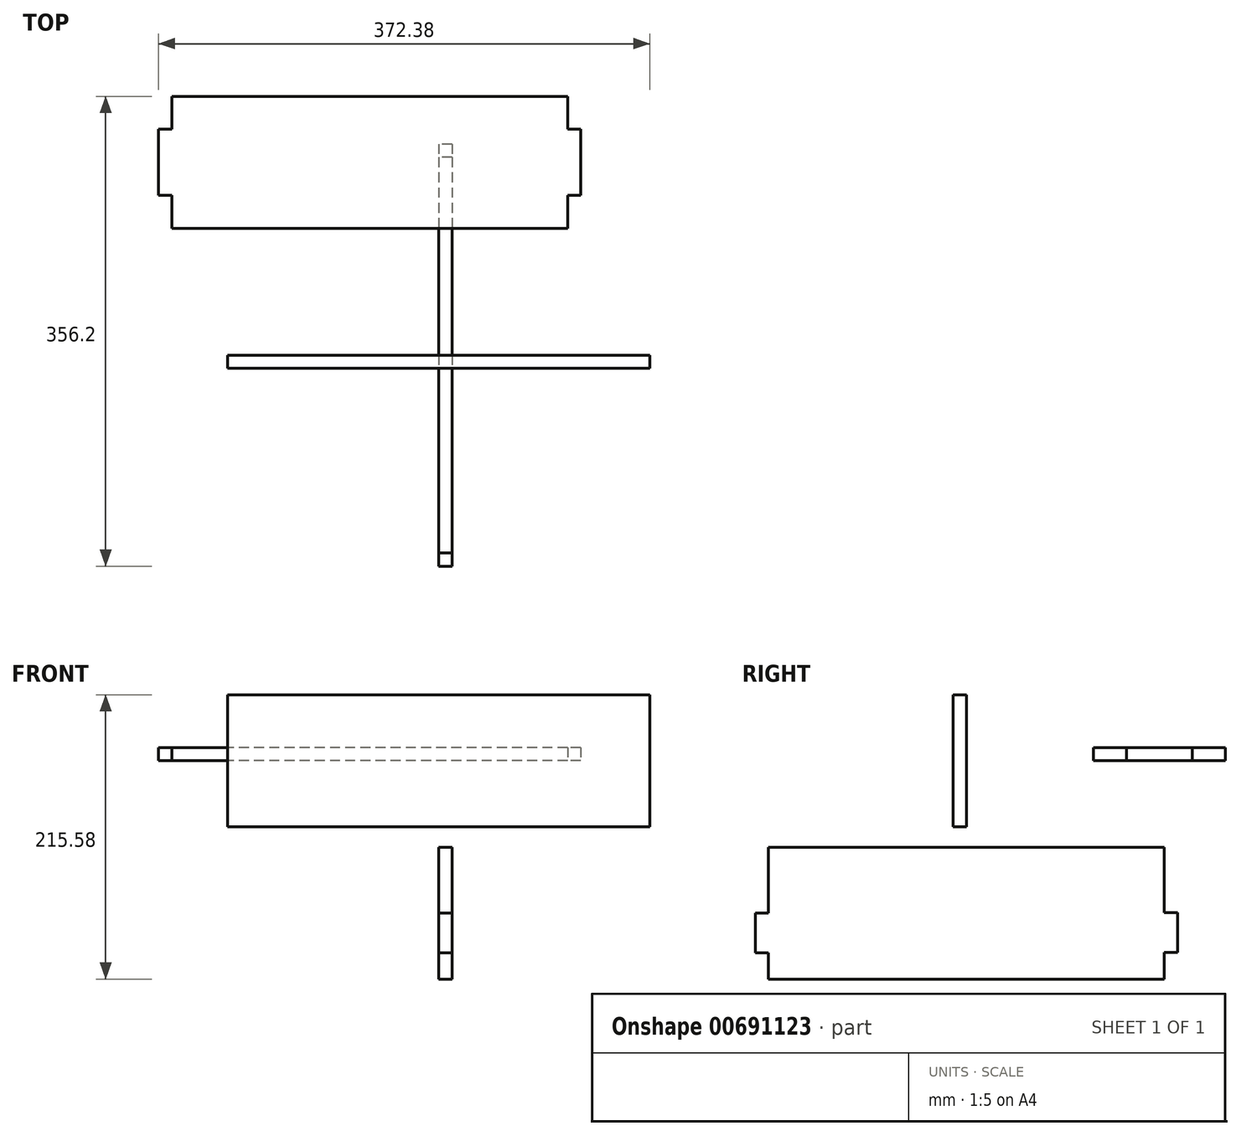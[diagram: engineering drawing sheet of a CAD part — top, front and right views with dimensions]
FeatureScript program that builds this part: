
annotation { "Feature Type Name" : "Feature", "Feature Type Description" : "" }
export const myFeature = defineFeature(function(context is Context, id is Id, definition is map)
    precondition{}
    {
        {
            var Q0;
            Q0=qCreatedBy(makeId("Front.planeOp"),FACE);
            var sketch = newSketch(context, id + "F0", { "sketchPlane" : qUnion([Q0])});
            skLineSegment(sketch, "E0.bottom", {"start": v(160, -50) * mm, "end": v(-160, -50) * mm});
            skLineSegment(sketch, "E0.top", {"start": v(160, 50) * mm, "end": v(-160, 50) * mm});
            skLineSegment(sketch, "E0.left", {"start": v(160, -50) * mm, "end": v(160, 50) * mm});
            skLineSegment(sketch, "E0.right", {"start": v(-160, -50) * mm, "end": v(-160, 50) * mm});
            skPoint(sketch, "E0.middle", {"position": v(0, 0) * mm});
            skSolve(sketch);
        }
        {
            var Q0;
            Q0=makeQuery(id+"F0.imprint","IMPRINT",FACE,{"disambiguationData":[TD([[makeQuery(id+"F0.imprint","IMPRINT",EDGE,{"derivedFrom":sQuery(id+"F0.wireOp",EDGE,"E0.bottom")}),-1.0]])]});
            extrude(context, id + "F1", {"entities" : qUnion([Q0]), "depth" : 10 * mm, "offsetDistance" : 25 * mm});
        }
        {
            var Q0;
            Q0=qCreatedBy(makeId("Top.planeOp"),FACE);
            var sketch = newSketch(context, id + "F2", { "sketchPlane" : qUnion([Q0])});
            skLineSegment(sketch, "E1.bottom", {"start": v(107.62, 96.25) * mm, "end": v(-212.38, 96.25) * mm});
            skLineSegment(sketch, "E1.top", {"start": v(107.62, 196.25) * mm, "end": v(-212.38, 196.25) * mm});
            skLineSegment(sketch, "E1.left", {"start": v(107.62, 96.25) * mm, "end": v(107.62, 196.25) * mm});
            skLineSegment(sketch, "E1.right", {"start": v(-212.38, 96.25) * mm, "end": v(-212.38, 196.25) * mm});
            skPoint(sketch, "E1.middle", {"position": v(-52.38, 146.25) * mm});
            skLineSegment(sketch, "E2", {"start": v(-202.38, 196.25) * mm, "end": v(-202.38, 96.25) * mm});
            skLineSegment(sketch, "E3", {"start": v(97.62, 196.25) * mm, "end": v(97.62, 96.25) * mm});
            skLineSegment(sketch, "E4", {"start": v(-212.38, 171.25) * mm, "end": v(-202.38, 171.25) * mm});
            skLineSegment(sketch, "E5", {"start": v(-212.38, 121.25) * mm, "end": v(-202.38, 121.25) * mm});
            skLineSegment(sketch, "E6.MirrorCS", {"start": v(107.62, 171.25) * mm, "end": v(97.62, 171.25) * mm});
            skLineSegment(sketch, "E7.MirrorCS", {"start": v(107.62, 121.25) * mm, "end": v(97.62, 121.25) * mm});
            skSolve(sketch);
        }
        {
            var Q0;
            {var subQ0=sQuery(id+"F2.wireOp",EDGE,"E2");var subQ5=sQuery(id+"F2.wireOp",EDGE,"E1.bottom");var subQ6=makeQuery(id+"F2.imprint","INTERSECT",VERTEX,{"derivedFrom":[subQ5,subQ0]});Q0=makeQuery(id+"F2.imprint","IMPRINT",FACE,{"disambiguationData":[TD([[makeQuery(id+"F2.imprint","IMPRINT",EDGE,{"disambiguationData":[TD([[subQ6,1.0]])],"derivedFrom":subQ5}),-1.0]])]});}
            var Q1;
            {var subQ0=sQuery(id+"F2.wireOp",EDGE,"E4");Q1=makeQuery(id+"F2.imprint","IMPRINT",FACE,{"disambiguationData":[TD([[makeQuery(id+"F2.imprint","IMPRINT",EDGE,{"derivedFrom":subQ0}),-1.0]])]});}
            var Q2;
            {var subQ0=sQuery(id+"F2.wireOp",EDGE,"E6.MirrorCS");Q2=makeQuery(id+"F2.imprint","IMPRINT",FACE,{"disambiguationData":[TD([[makeQuery(id+"F2.imprint","IMPRINT",EDGE,{"derivedFrom":subQ0}),1.0]])]});}
            extrude(context, id + "F3", {"entities" : qUnion([Q0, Q1, Q2]), "depth" : 10 * mm, "offsetDistance" : 25 * mm});
        }
        {
            var Q0;
            Q0=qCreatedBy(makeId("Right.planeOp"),FACE);
            var sketch = newSketch(context, id + "F4", { "sketchPlane" : qUnion([Q0])});
            skLineSegment(sketch, "E8.bottom", {"start": v(150.05, -165.58) * mm, "end": v(-149.95, -165.58) * mm});
            skLineSegment(sketch, "E8.top", {"start": v(149.95, -65.58) * mm, "end": v(-149.95, -65.58) * mm});
            skLineSegment(sketch, "E8.left", {"start": v(160.05, -145.28) * mm, "end": v(160.05, -115.28) * mm});
            skLineSegment(sketch, "E8.right", {"start": v(-159.95, -145.58) * mm, "end": v(-159.95, -115.58) * mm});
            skPoint(sketch, "E8.middle", {"position": v(0.05, -115.58) * mm});
            skLineSegment(sketch, "E9", {"start": v(-149.95, -65.58) * mm, "end": v(-149.95, -115.58) * mm});
            skLineSegment(sketch, "E10", {"start": v(-159.95, -145.58) * mm, "end": v(-149.95, -145.58) * mm});
            skLineSegment(sketch, "E11", {"start": v(-159.95, -115.58) * mm, "end": v(-149.95, -115.58) * mm});
            skLineSegment(sketch, "E12.MirrorCS", {"start": v(160.05, -115.28) * mm, "end": v(150.05, -115.3) * mm});
            skLineSegment(sketch, "E13.MirrorCS", {"start": v(160.1, -145.28) * mm, "end": v(150.1, -145.3) * mm});
            skLineSegment(sketch, "E14", {"start": v(-159.95, -115.58) * mm, "end": v(-159.95, -145.58) * mm});
            skLineSegment(sketch, "E15", {"start": v(160.05, -115.28) * mm, "end": v(160.1, -145.28) * mm});
            skLineSegment(sketch, "E16", {"start": v(150.1, -145.3) * mm, "end": v(160.1, -145.28) * mm});
            skPoint(sketch, "E17.orphan", {"position": v(160.05, -65.58) * mm});
            skPoint(sketch, "E18.orphan", {"position": v(160.05, -165.58) * mm});
            skPoint(sketch, "E19.orphan", {"position": v(-159.95, -65.58) * mm});
            skPoint(sketch, "E20.orphan", {"position": v(-159.95, -165.58) * mm});
            skLineSegment(sketch, "E21", {"start": v(150.05, -115.3) * mm, "end": v(149.95, -65.58) * mm});
            skLineSegment(sketch, "E22", {"start": v(150.1, -145.3) * mm, "end": v(150.05, -165.58) * mm});
            skLineSegment(sketch, "E23.trimOffspring", {"start": v(-149.95, -145.58) * mm, "end": v(-149.95, -165.58) * mm});
            skSolve(sketch);
        }
        {
            var Q0;
            {var subQ0=sQuery(id+"F4.wireOp",EDGE,"E10");Q0=makeQuery(id+"F4.imprint","IMPRINT",FACE,{"disambiguationData":[TD([[makeQuery(id+"F4.imprint","IMPRINT",EDGE,{"derivedFrom":subQ0}),1.0]])]});}
            var Q1;
            {var subQ5=sQuery(id+"F4.wireOp",EDGE,"E12.MirrorCS");Q1=makeQuery(id+"F4.imprint","IMPRINT",FACE,{"disambiguationData":[TD([[makeQuery(id+"F4.imprint","IMPRINT",EDGE,{"derivedFrom":subQ5}),1.0]])]});}
            var Q2;
            {var subQ6=sQuery(id+"F4.wireOp",EDGE,"E8.left");var subQ7=sQuery(id+"F4.wireOp",EDGE,"E8.bottom");var subQ8=makeQuery(id+"F4.imprint","INTERSECT",VERTEX,{"derivedFrom":[subQ7,subQ6]});Q2=makeQuery(id+"F4.imprint","IMPRINT",FACE,{"disambiguationData":[TD([[makeQuery(id+"F4.imprint","IMPRINT",EDGE,{"disambiguationData":[TD([[subQ8,-1.0]])],"derivedFrom":subQ7}),-1.0]])]});}
            extrude(context, id + "F5", {"entities" : qUnion([Q0, Q1, Q2]), "depth" : 10 * mm, "offsetDistance" : 25 * mm});
        }
    });
